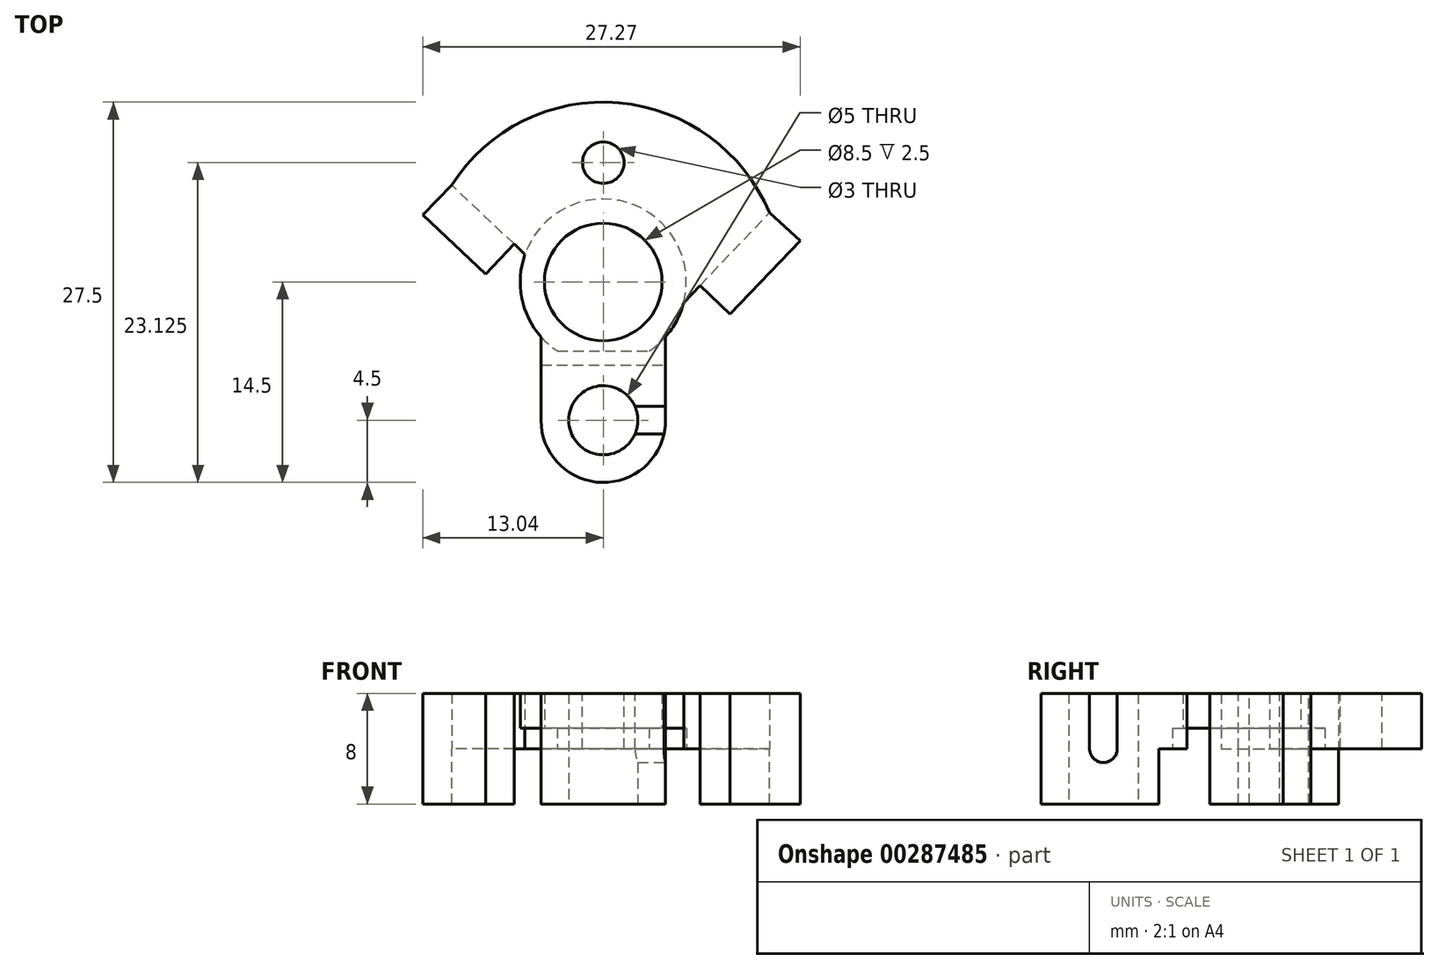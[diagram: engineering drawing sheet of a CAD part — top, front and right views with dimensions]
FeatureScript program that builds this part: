
annotation { "Feature Type Name" : "Feature", "Feature Type Description" : "" }
export const myFeature = defineFeature(function(context is Context, id is Id, definition is map)
    precondition{}
    {
        {
            var Q0;
            Q0=qCreatedBy(makeId("Top.planeOp"),FACE);
            var sketch = newSketch(context, id + "F0", { "sketchPlane" : qUnion([Q0])});
            skArc(sketch, "E0", {"start": v(3.32, -5) * mm, "mid": v(0, 6) * mm, "end": v(-3.32, -5) * mm});
            skLineSegment(sketch, "E1", {"start": v(-3.32, -5) * mm, "end": v(3.32, -5) * mm});
            skPoint(sketch, "E2", {"position": v(0, 6) * mm});
            skLineSegment(sketch, "E3", {"start": v(-4.5, -3.97) * mm, "end": v(-4.5, -10) * mm});
            skLineSegment(sketch, "E4", {"start": v(4.5, -3.97) * mm, "end": v(4.5, -10) * mm});
            skCircle(sketch, "E5", {"center": v(0, -10) * mm, "radius": 2.5 * mm});
            skPoint(sketch, "E5.centerSnap0", {"position": v(0, -5) * mm});
            skArc(sketch, "E6", {"start": v(12, 5) * mm, "mid": v(1.13, 12.95) * mm, "end": v(-10.95, 7) * mm});
            skLineSegment(sketch, "E7", {"start": v(-5.66, 2) * mm, "end": v(-10.95, 7) * mm});
            skLineSegment(sketch, "E8", {"start": v(5.8, -1.5) * mm, "end": v(12, 5) * mm});
            skArc(sketch, "E9", {"start": v(-4.5, -10) * mm, "mid": v(0, -14.5) * mm, "end": v(4.5, -10) * mm});
            skLineSegment(sketch, "E10", {"start": v(-4.5, -6) * mm, "end": v(4.5, -6) * mm});
            skSolve(sketch);
        }
        {
            var Q0;
            Q0=makeQuery(id+"F0.imprint","IMPRINT",FACE,{"disambiguationData":[TD([[makeQuery(id+"F0.imprint","IMPRINT",EDGE,{"derivedFrom":sQuery(id+"F0.wireOp",EDGE,"E6")}),1.0]])]});
            var Q1;
            {var subQ5=sQuery(id+"F0.wireOp",EDGE,"E1");Q1=makeQuery(id+"F0.imprint","IMPRINT",FACE,{"disambiguationData":[TD([[makeQuery(id+"F0.imprint","IMPRINT",EDGE,{"derivedFrom":subQ5}),1.0]])]});}
            var Q2;
            {var subQ1=sQuery(id+"F0.wireOp",EDGE,"E1");Q2=makeQuery(id+"F0.imprint","IMPRINT",FACE,{"disambiguationData":[TD([[makeQuery(id+"F0.imprint","IMPRINT",EDGE,{"derivedFrom":subQ1}),-1.0]])]});}
            var Q3;
            Q3=makeQuery(id+"F0.imprint","IMPRINT",FACE,{"disambiguationData":[TD([[makeQuery(id+"F0.imprint","IMPRINT",EDGE,{"derivedFrom":sQuery(id+"F0.wireOp",EDGE,"E5")}),-1.0]])]});
            extrude(context, id + "F1", {"entities" : qUnion([Q0, Q1, Q2, Q3]), "depth" : 4 * mm});
        }
        {
            var Q0;
            Q0=makeQuery(id+"F0.imprint","IMPRINT",FACE,{"disambiguationData":[TD([[makeQuery(id+"F0.imprint","IMPRINT",EDGE,{"derivedFrom":sQuery(id+"F0.wireOp",EDGE,"E5")}),-1.0]])]});
            extrude(context, id + "F2", {"entities" : qUnion([Q0]), "operationType" : NewBodyOperationType.ADD, "oppositeDirection" : true, "depth" : 4 * mm});
        }
        {
            var Q0;
            {var subQ5=sQuery(id+"F0.wireOp",EDGE,"E1");Q0=makeQuery(id+"F0.imprint","IMPRINT",FACE,{"disambiguationData":[TD([[makeQuery(id+"F0.imprint","IMPRINT",EDGE,{"derivedFrom":subQ5}),1.0]])]});}
            var sketch = newSketch(context, id + "F3", { "sketchPlane" : qUnion([Q0])});
            skLineSegment(sketch, "E11.0", {"start": v(9.17, -2.32) * mm, "end": v(14.23, 2.99) * mm});
            skArc(sketch, "E12.0", {"start": v(3.32, -5) * mm, "mid": v(0, 6) * mm, "end": v(-3.32, -5) * mm});
            skLineSegment(sketch, "E13.0", {"start": v(5.8, -1.5) * mm, "end": v(12, 5) * mm});
            skLineSegment(sketch, "E14.0", {"start": v(4.5, -3.97) * mm, "end": v(4.5, -10) * mm});
            skLineSegment(sketch, "E15.0", {"start": v(-5.66, 2) * mm, "end": v(-10.95, 7) * mm});
            skLineSegment(sketch, "E16.0", {"start": v(-8.5, 0.56) * mm, "end": v(-13.04, 4.84) * mm});
            skLineSegment(sketch, "E17", {"start": v(14.23, 2.99) * mm, "end": v(12, 5) * mm});
            skLineSegment(sketch, "E18", {"start": v(-13.04, 4.84) * mm, "end": v(-10.95, 7) * mm});
            skArc(sketch, "E19", {"start": v(-6.44, 2.74) * mm, "mid": v(1.52, 6.83) * mm, "end": v(7, -0.25) * mm});
            skLineSegment(sketch, "E20", {"start": v(7, -0.25) * mm, "end": v(9.17, -2.32) * mm});
            skLineSegment(sketch, "E21", {"start": v(-6.44, 2.74) * mm, "end": v(-8.5, 0.56) * mm});
            skSolve(sketch);
        }
        {
            var Q0;
            Q0=makeQuery(id+"F3.imprint","IMPRINT",FACE,{"disambiguationData":[TD([[makeQuery(id+"F3.imprint","IMPRINT",EDGE,{"derivedFrom":sQuery(id+"F3.wireOp",EDGE,"E11.0")}),1.0]])]});
            var Q1;
            Q1=makeQuery(id+"F3.imprint","IMPRINT",FACE,{"disambiguationData":[TD([[makeQuery(id+"F3.imprint","IMPRINT",EDGE,{"derivedFrom":sQuery(id+"F3.wireOp",EDGE,"E15.0")}),1.0]])]});
            var Q2;
            {var subQ1=sQuery(id+"F3.wireOp",EDGE,"E16.0");Q2=makeQuery(id+"F3.imprint","IMPRINT",FACE,{"disambiguationData":[TD([[makeQuery(id+"F3.imprint","IMPRINT",EDGE,{"derivedFrom":subQ1}),-1.0]])]});}
            var Q3;
            {var subQ0=sQuery(id+"F3.wireOp",EDGE,"XfcFJEv5-znfx-dZly-SWym-98SlYmC9ljbC");var subQ3=sQuery(id+"F3.wireOp",EDGE,"e9QkvNZh-2jtj-YoAd-HKKd-2TcBkycMxzSG");var subQ5=makeQuery(id+"F3.imprint","INTERSECT",VERTEX,{"derivedFrom":[subQ0,subQ3]});Q3=makeQuery(id+"F3.imprint","IMPRINT",FACE,{"disambiguationData":[TD([[makeQuery(id+"F3.imprint","IMPRINT",EDGE,{"disambiguationData":[TD([[subQ5,-1.0]])],"derivedFrom":subQ3}),1.0]])]});}
            extrude(context, id + "F4", {"entities" : qUnion([Q0, Q1, Q2, Q3]), "operationType" : NewBodyOperationType.ADD, "oppositeDirection" : true, "depth" : 4 * mm, "hasSecondDirection" : true, "secondDirectionOppositeDirection" : false, "secondDirectionDepth" : 4 * mm});
        }
        {
            var Q0;
            {var subQ5=sQuery(id+"F3.wireOp",EDGE,"E19");Q0=makeQuery(id+"F3.imprint","IMPRINT",FACE,{"disambiguationData":[TD([[makeQuery(id+"F3.imprint","IMPRINT",EDGE,{"derivedFrom":subQ5}),-1.0]])]});}
            var Q1;
            {var subQ5=makeQuery(id+"F0.imprint","IMPRINT",EDGE,{"derivedFrom":sQuery(id+"F0.wireOp",EDGE,"E1")});Q1=makeQuery(id+"F3.imprint","IMPRINT",FACE,{"disambiguationData":[TD([[makeQuery(id+"F3.imprint","IMPRINT",EDGE,{"derivedFrom":subQ5}),1.0]])]});}
            extrude(context, id + "F5", {"entities" : qUnion([Q0, Q1]), "operationType" : NewBodyOperationType.REMOVE, "depth" : 1.5 * mm});
        }
        {
            var Q0;
            Q0=sQuery(id+"F0.wireOp",VERTEX,"E0.center");
            var Q1;
            Q1=makeQuery(id+"F1.opExtrude","SWEPT_BODY",BODY,{"disambiguationData":[OSD([sQuery(id+"F0.wireOp",EDGE,"E0"),sQuery(id+"F0.wireOp",EDGE,"E3"),sQuery(id+"F0.wireOp",EDGE,"E4"),sQuery(id+"F0.wireOp",EDGE,"E5"),sQuery(id+"F0.wireOp",EDGE,"E6"),sQuery(id+"F0.wireOp",EDGE,"E7"),sQuery(id+"F0.wireOp",EDGE,"E8"),sQuery(id+"F0.wireOp",EDGE,"E9")])]});
            hole(context, id + "F6", {"style" : HoleStyle.SIMPLE, "endStyle" : HoleEndStyle.THROUGH, "oppositeDirection" : true, "holeDiameter" : 8.5 * mm, "tappedDepth" : 12 * mm, "tapClearance" : 3, "locations" : qUnion([Q0]), "scope" : qUnion([Q1])});
        }
        {
            var Q0;
            Q0=makeQuery(id+"F4.boolean.opBoolean","MERGE",FACE,{"derivedFrom":[makeQuery(id+"F1.opExtrude","CAP_FACE",FACE,{"disambiguationData":[OSD([sQuery(id+"F0.wireOp",EDGE,"E0"),sQuery(id+"F0.wireOp",EDGE,"E3"),sQuery(id+"F0.wireOp",EDGE,"E4"),sQuery(id+"F0.wireOp",EDGE,"E5"),sQuery(id+"F0.wireOp",EDGE,"E6"),sQuery(id+"F0.wireOp",EDGE,"E7"),sQuery(id+"F0.wireOp",EDGE,"E8"),sQuery(id+"F0.wireOp",EDGE,"E9")])],"isStart":false}),makeQuery(id+"F4.opExtrude","CAP_FACE",FACE,{"disambiguationData":[OSD([sQuery(id+"F3.wireOp",EDGE,"E11.0"),sQuery(id+"F3.wireOp",EDGE,"E13.0"),sQuery(id+"F3.wireOp",EDGE,"E17"),sQuery(id+"F3.wireOp",EDGE,"XfcFJEv5-znfx-dZly-SWym-98SlYmC9ljbC")])],"isStart":true}),makeQuery(id+"F4.opExtrude","CAP_FACE",FACE,{"disambiguationData":[OSD([sQuery(id+"F3.wireOp",EDGE,"E15.0"),sQuery(id+"F3.wireOp",EDGE,"E16.0"),sQuery(id+"F3.wireOp",EDGE,"GuNQAwtB-KBeB-Tbym-2g7i-GYj6E9QDXpPe"),sQuery(id+"F3.wireOp",EDGE,"E18")])],"isStart":true})]});
            var sketch = newSketch(context, id + "F7", { "sketchPlane" : qUnion([Q0])});
            skLineSegment(sketch, "E22", {"start": v(2.3, -9) * mm, "end": v(4.5, -9) * mm});
            skLineSegment(sketch, "E23", {"start": v(2.3, -11) * mm, "end": v(4.39, -11) * mm});
            skSolve(sketch);
        }
        {
            var Q0;
            {var subQ3=sQuery(id+"F7.wireOp",EDGE,"E22");Q0=makeQuery(id+"F7.imprint","IMPRINT",FACE,{"disambiguationData":[TD([[makeQuery(id+"F7.imprint","IMPRINT",EDGE,{"derivedFrom":subQ3}),-1.0]])]});}
            extrude(context, id + "F8", {"entities" : qUnion([Q0]), "operationType" : NewBodyOperationType.REMOVE, "oppositeDirection" : true, "depth" : 5 * mm});
        }
        {
            var Q0;
            Q0=makeQuery(id+"F8.boolean.opBoolean","COPY",EDGE,{"derivedFrom":makeQuery(id+"F8.opExtrude","CAP_EDGE",EDGE,{"disambiguationData":[OSD([sQuery(id+"F7.wireOp",EDGE,"E23")])],"isStart":false})});
            var Q1;
            Q1=makeQuery(id+"F8.boolean.opBoolean","COPY",EDGE,{"derivedFrom":makeQuery(id+"F8.opExtrude","CAP_EDGE",EDGE,{"disambiguationData":[OSD([sQuery(id+"F7.wireOp",EDGE,"E22")])],"isStart":false})});
            fillet(context, id + "F9", {"entities" : qUnion([Q0, Q1]), "radius" : 1 * mm, "tangentPropagation" : true, "allowEdgeOverflow" : false});
        }
        {
            var Q0;
            Q0=makeQuery(id+"F4.boolean.opBoolean","MERGE",FACE,{"derivedFrom":[makeQuery(id+"F1.opExtrude","CAP_FACE",FACE,{"disambiguationData":[OSD([sQuery(id+"F0.wireOp",EDGE,"E0"),sQuery(id+"F0.wireOp",EDGE,"E3"),sQuery(id+"F0.wireOp",EDGE,"E4"),sQuery(id+"F0.wireOp",EDGE,"E5"),sQuery(id+"F0.wireOp",EDGE,"E6"),sQuery(id+"F0.wireOp",EDGE,"E7"),sQuery(id+"F0.wireOp",EDGE,"E8"),sQuery(id+"F0.wireOp",EDGE,"E9")])],"isStart":false}),makeQuery(id+"F4.opExtrude","CAP_FACE",FACE,{"disambiguationData":[OSD([sQuery(id+"F3.wireOp",EDGE,"E11.0"),sQuery(id+"F3.wireOp",EDGE,"E13.0"),sQuery(id+"F3.wireOp",EDGE,"E17"),sQuery(id+"F3.wireOp",EDGE,"XfcFJEv5-znfx-dZly-SWym-98SlYmC9ljbC")])],"isStart":true}),makeQuery(id+"F4.opExtrude","CAP_FACE",FACE,{"disambiguationData":[OSD([sQuery(id+"F3.wireOp",EDGE,"E15.0"),sQuery(id+"F3.wireOp",EDGE,"E16.0"),sQuery(id+"F3.wireOp",EDGE,"GuNQAwtB-KBeB-Tbym-2g7i-GYj6E9QDXpPe"),sQuery(id+"F3.wireOp",EDGE,"E18")])],"isStart":true})]});
            var sketch = newSketch(context, id + "F10", { "sketchPlane" : qUnion([Q0])});
            skLineSegment(sketch, "E24", {"start": v(0, 13) * mm, "end": v(0, 4.25) * mm, "construction": true});
            skPoint(sketch, "E25", {"position": v(0, 8.63) * mm});
            skSolve(sketch);
        }
        {
            var Q0;
            Q0=sQuery(id+"F10.wireOp",VERTEX,"E25");
            var Q1;
            Q1=makeQuery(id+"F1.opExtrude","SWEPT_BODY",BODY,{"disambiguationData":[OSD([sQuery(id+"F0.wireOp",EDGE,"E0"),sQuery(id+"F0.wireOp",EDGE,"E3"),sQuery(id+"F0.wireOp",EDGE,"E4"),sQuery(id+"F0.wireOp",EDGE,"E5"),sQuery(id+"F0.wireOp",EDGE,"E6"),sQuery(id+"F0.wireOp",EDGE,"E7"),sQuery(id+"F0.wireOp",EDGE,"E8"),sQuery(id+"F0.wireOp",EDGE,"E9")])]});
            hole(context, id + "F11", {"style" : HoleStyle.SIMPLE, "endStyle" : HoleEndStyle.THROUGH, "holeDiameter" : 3 * mm, "tappedDepth" : 12 * mm, "tapClearance" : 3, "locations" : qUnion([Q0]), "scope" : qUnion([Q1])});
        }
    });
